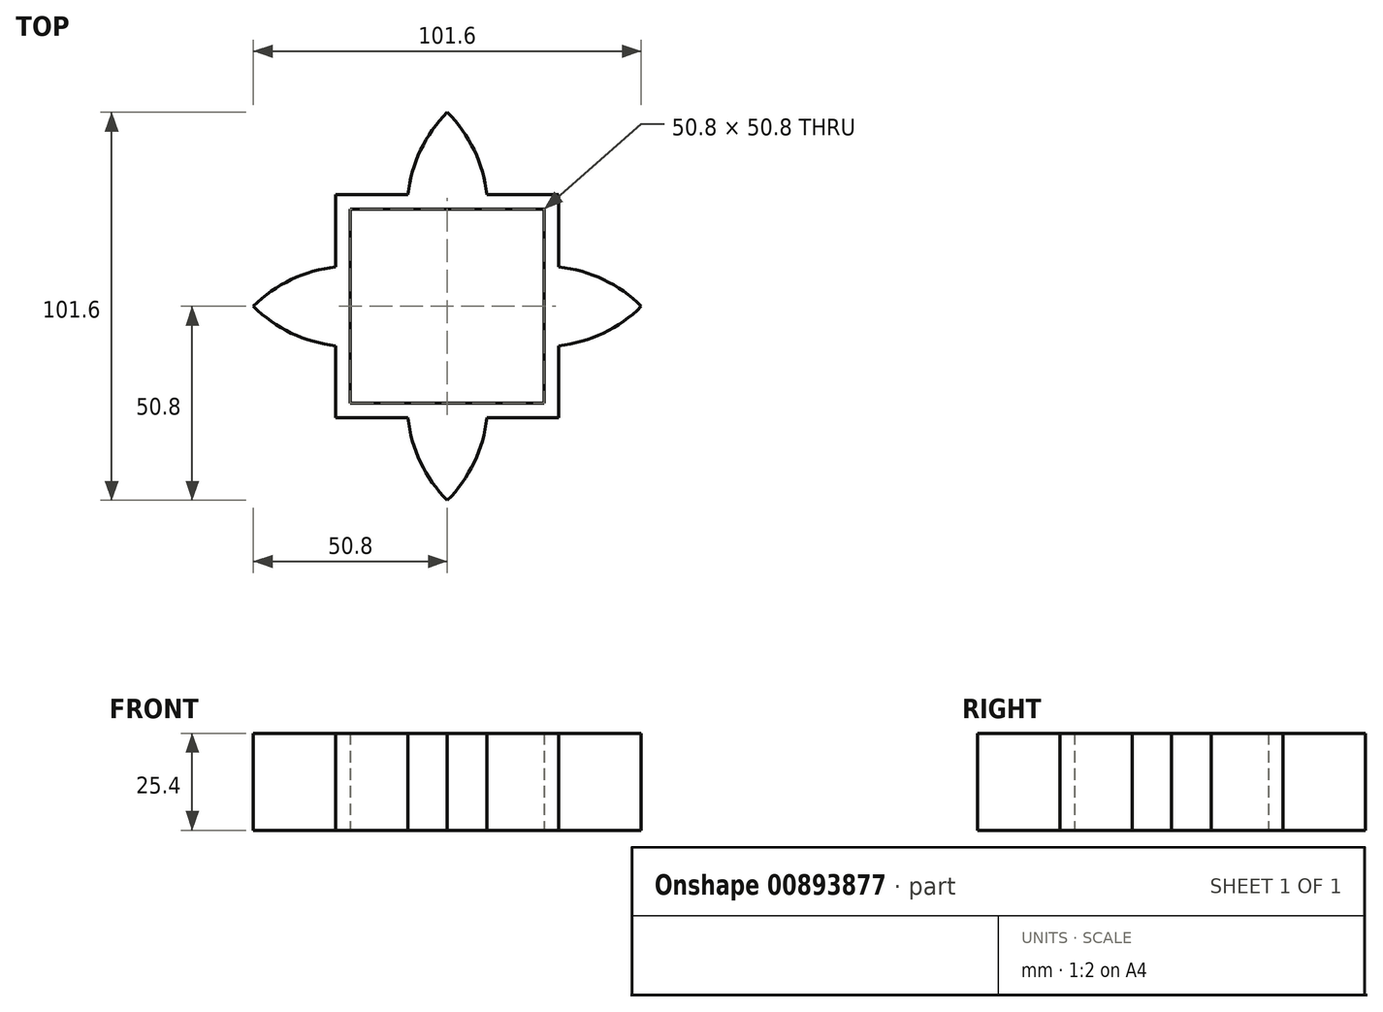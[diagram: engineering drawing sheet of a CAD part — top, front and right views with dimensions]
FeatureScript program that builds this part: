
annotation { "Feature Type Name" : "Feature", "Feature Type Description" : "" }
export const myFeature = defineFeature(function(context is Context, id is Id, definition is map)
    precondition{}
    {
        {
            var Q0;
            Q0=qCreatedBy(makeId("Top.planeOp"),FACE);
            var sketch = newSketch(context, id + "F0", { "sketchPlane" : qUnion([Q0])});
            skLineSegment(sketch, "E0.bottom", {"start": v(0, 50.8) * mm, "end": v(0, 50.8) * mm});
            skLineSegment(sketch, "E0.top", {"start": v(0, -50.8) * mm, "end": v(0, -50.8) * mm});
            skLineSegment(sketch, "E0.left", {"start": v(-50.8, 0) * mm, "end": v(-50.8, 0) * mm});
            skLineSegment(sketch, "E0.right", {"start": v(50.8, 0) * mm, "end": v(50.8, 0) * mm});
            skPoint(sketch, "E0.middle", {"position": v(0, 0) * mm});
            skPoint(sketch, "E1.visualSharp", {"position": v(-50.8, 50.8) * mm});
            skArc(sketch, "E1.filletArc", {"start": v(0, 50.8) * mm, "mid": v(-35.92, 35.92) * mm, "end": v(-50.8, 0) * mm});
            skPoint(sketch, "E2.visualSharp", {"position": v(-50.8, -50.8) * mm});
            skArc(sketch, "E2.filletArc", {"start": v(-50.8, 0) * mm, "mid": v(-35.92, -35.92) * mm, "end": v(0, -50.8) * mm});
            skPoint(sketch, "E3.visualSharp", {"position": v(50.8, -50.8) * mm});
            skArc(sketch, "E3.filletArc", {"start": v(0, -50.8) * mm, "mid": v(35.92, -35.92) * mm, "end": v(50.8, 0) * mm});
            skPoint(sketch, "E4.visualSharp", {"position": v(50.8, 50.8) * mm});
            skArc(sketch, "E4.filletArc", {"start": v(50.8, 0) * mm, "mid": v(35.92, 35.92) * mm, "end": v(0, 50.8) * mm});
            skArc(sketch, "E5", {"start": v(0, 50.8) * mm, "mid": v(0, 0) * mm, "end": v(50.8, 0) * mm});
            skArc(sketch, "E6", {"start": v(-50.8, 0) * mm, "mid": v(0, 0) * mm, "end": v(0, 50.8) * mm});
            skArc(sketch, "E7", {"start": v(0, -50.8) * mm, "mid": v(0, 0) * mm, "end": v(-50.8, 0) * mm});
            skArc(sketch, "E8", {"start": v(50.8, 0) * mm, "mid": v(0, 0) * mm, "end": v(0, -50.8) * mm});
            skLineSegment(sketch, "E9.bottom", {"start": v(-25.4, 25.4) * mm, "end": v(25.4, 25.4) * mm});
            skLineSegment(sketch, "E9.top", {"start": v(-25.4, -25.4) * mm, "end": v(25.4, -25.4) * mm});
            skLineSegment(sketch, "E9.left", {"start": v(-25.4, 25.4) * mm, "end": v(-25.4, -25.4) * mm});
            skLineSegment(sketch, "E9.right", {"start": v(25.4, 25.4) * mm, "end": v(25.4, -25.4) * mm});
            skLineSegment(sketch, "E10.0", {"start": v(-29.21, 29.21) * mm, "end": v(29.21, 29.21) * mm});
            skLineSegment(sketch, "E10.1", {"start": v(-29.21, 29.21) * mm, "end": v(-29.21, -29.21) * mm});
            skLineSegment(sketch, "E10.2", {"start": v(-29.21, -29.21) * mm, "end": v(29.21, -29.21) * mm});
            skLineSegment(sketch, "E10.3", {"start": v(29.21, 29.21) * mm, "end": v(29.21, -29.21) * mm});
            skSolve(sketch);
        }
        {
            var Q0;
            {var subQ1=sQuery(id+"F0.wireOp",EDGE,"E6");var subQ3=sQuery(id+"F0.wireOp",EDGE,"E10.1");var subQ4=makeQuery(id+"F0.imprint","INTERSECT",VERTEX,{"derivedFrom":[subQ1,subQ3]});Q0=makeQuery(id+"F0.imprint","IMPRINT",FACE,{"disambiguationData":[TD([[makeQuery(id+"F0.imprint","IMPRINT",EDGE,{"disambiguationData":[TD([[subQ4,1.0]])],"derivedFrom":subQ3}),-1.0]])]});}
            var Q1;
            {var subQ1=sQuery(id+"F0.wireOp",EDGE,"E5");var subQ3=sQuery(id+"F0.wireOp",EDGE,"E10.0");var subQ4=makeQuery(id+"F0.imprint","INTERSECT",VERTEX,{"derivedFrom":[subQ1,subQ3]});Q1=makeQuery(id+"F0.imprint","IMPRINT",FACE,{"disambiguationData":[TD([[makeQuery(id+"F0.imprint","IMPRINT",EDGE,{"disambiguationData":[TD([[subQ4,-1.0]])],"derivedFrom":subQ3}),1.0]])]});}
            var Q2;
            {var subQ1=sQuery(id+"F0.wireOp",EDGE,"E5");var subQ3=sQuery(id+"F0.wireOp",EDGE,"E10.3");var subQ4=makeQuery(id+"F0.imprint","INTERSECT",VERTEX,{"derivedFrom":[subQ1,subQ3]});Q2=makeQuery(id+"F0.imprint","IMPRINT",FACE,{"disambiguationData":[TD([[makeQuery(id+"F0.imprint","IMPRINT",EDGE,{"disambiguationData":[TD([[subQ4,1.0]])],"derivedFrom":subQ3}),1.0]])]});}
            var Q3;
            {var subQ1=sQuery(id+"F0.wireOp",EDGE,"E7");var subQ3=sQuery(id+"F0.wireOp",EDGE,"E10.2");var subQ4=makeQuery(id+"F0.imprint","INTERSECT",VERTEX,{"derivedFrom":[subQ1,subQ3]});Q3=makeQuery(id+"F0.imprint","IMPRINT",FACE,{"disambiguationData":[TD([[makeQuery(id+"F0.imprint","IMPRINT",EDGE,{"disambiguationData":[TD([[subQ4,1.0]])],"derivedFrom":subQ3}),-1.0]])]});}
            var Q4;
            {var subQ3=sQuery(id+"F0.wireOp",EDGE,"E6");var subQ9=sQuery(id+"F0.wireOp",EDGE,"E10.1");var subQ10=makeQuery(id+"F0.imprint","INTERSECT",VERTEX,{"derivedFrom":[subQ3,subQ9]});Q4=makeQuery(id+"F0.imprint","IMPRINT",FACE,{"disambiguationData":[TD([[makeQuery(id+"F0.imprint","IMPRINT",EDGE,{"disambiguationData":[TD([[subQ10,-1.0]])],"derivedFrom":subQ3}),-1.0]])]});}
            var Q5;
            {var subQ0=sQuery(id+"F0.wireOp",EDGE,"E10.1");var subQ1=sQuery(id+"F0.wireOp",EDGE,"E6");var subQ2=makeQuery(id+"F0.imprint","INTERSECT",VERTEX,{"derivedFrom":[subQ1,subQ0]});Q5=makeQuery(id+"F0.imprint","IMPRINT",FACE,{"disambiguationData":[TD([[makeQuery(id+"F0.imprint","IMPRINT",EDGE,{"disambiguationData":[TD([[subQ2,-1.0]])],"derivedFrom":subQ1}),1.0]])]});}
            var Q6;
            {var subQ5=sQuery(id+"F0.wireOp",EDGE,"E5");var subQ9=sQuery(id+"F0.wireOp",EDGE,"E10.0");var subQ10=makeQuery(id+"F0.imprint","INTERSECT",VERTEX,{"derivedFrom":[subQ5,subQ9]});Q6=makeQuery(id+"F0.imprint","IMPRINT",FACE,{"disambiguationData":[TD([[makeQuery(id+"F0.imprint","IMPRINT",EDGE,{"disambiguationData":[TD([[subQ10,-1.0]])],"derivedFrom":subQ5}),-1.0]])]});}
            var Q7;
            {var subQ0=sQuery(id+"F0.wireOp",EDGE,"E10.0");var subQ1=sQuery(id+"F0.wireOp",EDGE,"E5");var subQ2=makeQuery(id+"F0.imprint","INTERSECT",VERTEX,{"derivedFrom":[subQ1,subQ0]});Q7=makeQuery(id+"F0.imprint","IMPRINT",FACE,{"disambiguationData":[TD([[makeQuery(id+"F0.imprint","IMPRINT",EDGE,{"disambiguationData":[TD([[subQ2,-1.0]])],"derivedFrom":subQ1}),1.0]])]});}
            var Q8;
            {var subQ1=sQuery(id+"F0.wireOp",EDGE,"E9.bottom");var subQ5=sQuery(id+"F0.wireOp",EDGE,"E6");var subQ6=makeQuery(id+"F0.imprint","INTERSECT",VERTEX,{"derivedFrom":[subQ5,subQ1]});Q8=makeQuery(id+"F0.imprint","IMPRINT",FACE,{"disambiguationData":[TD([[makeQuery(id+"F0.imprint","IMPRINT",EDGE,{"disambiguationData":[TD([[subQ6,-1.0]])],"derivedFrom":subQ5}),-1.0]])]});}
            var Q9;
            {var subQ0=sQuery(id+"F0.wireOp",EDGE,"E9.right");var subQ3=sQuery(id+"F0.wireOp",EDGE,"E5");var subQ4=makeQuery(id+"F0.imprint","INTERSECT",VERTEX,{"derivedFrom":[subQ3,subQ0]});Q9=makeQuery(id+"F0.imprint","IMPRINT",FACE,{"disambiguationData":[TD([[makeQuery(id+"F0.imprint","IMPRINT",EDGE,{"disambiguationData":[TD([[subQ4,-1.0]])],"derivedFrom":subQ3}),-1.0]])]});}
            var Q10;
            {var subQ0=sQuery(id+"F0.wireOp",EDGE,"E9.right");var subQ1=sQuery(id+"F0.wireOp",EDGE,"E5");var subQ2=makeQuery(id+"F0.imprint","INTERSECT",VERTEX,{"derivedFrom":[subQ1,subQ0]});Q10=makeQuery(id+"F0.imprint","IMPRINT",FACE,{"disambiguationData":[TD([[makeQuery(id+"F0.imprint","IMPRINT",EDGE,{"disambiguationData":[TD([[subQ2,-1.0]])],"derivedFrom":subQ1}),1.0]])]});}
            var Q11;
            {var subQ0=sQuery(id+"F0.wireOp",EDGE,"E10.2");var subQ1=sQuery(id+"F0.wireOp",EDGE,"E7");var subQ2=makeQuery(id+"F0.imprint","INTERSECT",VERTEX,{"derivedFrom":[subQ1,subQ0]});Q11=makeQuery(id+"F0.imprint","IMPRINT",FACE,{"disambiguationData":[TD([[makeQuery(id+"F0.imprint","IMPRINT",EDGE,{"disambiguationData":[TD([[subQ2,-1.0]])],"derivedFrom":subQ1}),1.0]])]});}
            extrude(context, id + "F1", {"entities" : qUnion([Q0, Q1, Q2, Q3, Q4, Q5, Q6, Q7, Q8, Q9, Q10, Q11]), "depth" : 25.4 * mm, "offsetDistance" : 25.4 * mm});
        }
    });
